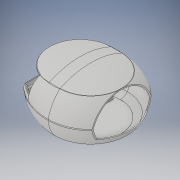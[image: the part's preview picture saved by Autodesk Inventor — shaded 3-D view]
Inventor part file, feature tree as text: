
AUTODESK INVENTOR PART (.ipt)
format: ipt  version: 2019 (Build 230136000, 136)  size: 2,652,672 bytes
history: native  units: mm
features: sketch x34, other x31, extrude x17, loft x12, pattern_linear x12, projected_geometry x12, fillet x10, mirror x5, revolve x3
ambient origin geometry x8: Origin, YZ Plane, XZ Plane, XY Plane, X Axis, Y Axis, Z Axis, Center Point
bodies: Body1 (feature_tree), Body2 (feature_tree)
feature tree (136):
  other  "голова"
  other  "Твердое тело1"
  sketch  "Эскиз1"
  extrude  "Выдавливание1"  Depth=42.3mm
  extrude  "Выдавливание2"  Depth=20.3mm
  extrude  "Выдавливание3"  Depth=40.0mm
  other  "РабПлоскость1"
  sketch  "Эскиз3"
  other  "РабПлоскость2"
  loft  "Лофт1"
  other  "РабПлоскость3"
  sketch  "Эскиз5"
  loft  "Лофт3"
  other  "РабПлоскость4"
  sketch  "Эскиз8"
  other  "РабПлоскость6"
  sketch  "Эскиз9"
  loft  "Лофт4"
  extrude  "Выдавливание4"  Depth=100.0mm
  mirror  "Зеркальное отражение1"
  loft  "Лофт5"
  loft  "Лофт6"
  loft  "Лофт7"
  sketch  "Эскиз11"
  extrude  "Выдавливание5"  Depth=20.0mm
  mirror  "Зеркальное отражение2"
  sketch  "Эскиз13"
  other  "РабПлоскость7"
  sketch  "Эскиз14"
  other  "РабПлоскость9"
  sketch  "Эскиз16"
  other  "РабПлоскость10"
  sketch  "Эскиз17"
  other  "РабПлоскость8"
  extrude  "Выдавливание6"  Depth=2.0mm TaperAngle=0.0deg
  loft  "Лофт8"
  mirror  "Зеркальное отражение3"
  other  "РабПлоскость11"
  revolve  "Вращение1"
  extrude  "Выдавливание7"  Depth=2.0mm
  loft  "Лофт9"
  loft  "Лофт10"
  other  "РабПлоскость12"
  sketch  "Эскиз20"
  sketch  "Эскиз21"
  sketch  "Эскиз22"
  loft  "Лофт11"
  loft  "Лофт12"
  mirror  "Зеркальное отражение4"
  other  "РабПлоскость13"
  loft  "Лофт13"
  extrude  "Выдавливание9"  Depth=50.0mm
  fillet  "Сопряжение1"  Radius=52.0mm
  fillet  "Сопряжение2"  Radius=2.0mm
  fillet  "Сопряжение3"  Radius=2.0mm
  fillet  "Сопряжение4"  Radius=46.0mm
  fillet  "Сопряжение5"  Radius=31.0mm
  fillet  "Сопряжение6"  Radius=30.0mm
  fillet  "Сопряжение7"  Radius=2.0mm
  extrude  "Выдавливание10"  Depth=2.0mm
  pattern_linear  "Прямоуг.массив1"  Spacing1=2.0mm  [1 undecoded]
  pattern_linear  "Прямоуг.массив2"  Spacing1=98.851581mm  [1 undecoded]
  pattern_linear  "Прямоуг.массив3"  Spacing1=40.790396mm  [1 undecoded]
  pattern_linear  "Прямоуг.массив4"  Spacing1=0.0mm  [1 undecoded]
  pattern_linear  "Прямоуг.массив5"  Spacing1=0.0mm  [1 undecoded]
  pattern_linear  "Прямоуг.массив6"  Spacing1=2.0mm  [1 undecoded]
  pattern_linear  "Прямоуг.массив7"  Spacing1=2.0mm  [1 undecoded]
  pattern_linear  "Прямоуг.массив8"  Spacing1=2.0mm  [1 undecoded]
  pattern_linear  "Прямоуг.массив9"  Spacing1=83.118457mm  [1 undecoded]
  pattern_linear  "Прямоуг.массив10"  Spacing1=1.99778mm  [1 undecoded]
  pattern_linear  "Прямоуг.массив11"  Spacing1=0.0mm  [1 undecoded]
  pattern_linear  "Прямоуг.массив12"  Spacing1=0.0mm  [1 undecoded]
  mirror  "Зеркальное отражение5"
  fillet  "Сопряжение8"  Radius=2.0mm
  fillet  "Сопряжение9"  Radius=2.0mm
  fillet  "Сопряжение10"  Radius=2.0mm
  extrude  "Выдавливание12"  Depth=53.0mm
  revolve  "Вращение2"
  extrude  "Выдавливание13"  Depth=2.0mm
  revolve  "Вращение3"
  other  "РабПлоскость14"
  sketch  "Эскиз35"
  extrude  "Выдавливание14"  TaperAngle=0.0deg  [1 undecoded]
  extrude  "Выдавливание15"  TaperAngle=0.0deg  [1 undecoded]
  other  "РабПлоскость15"
  extrude  "Выдавливание17"  TaperAngle=0.0deg  [1 undecoded]
  extrude  "Выдавливание20"  Depth=60.0mm TaperAngle=0.0deg
  sketch  "Эскиз47"
  extrude  "Выдавливание21"  TaperAngle=0.0deg  [1 undecoded]
  extrude  "Выдавливание22"  TaperAngle=0.0deg  [1 undecoded]
  sketch  "Эскиз2"
  sketch  "Эскиз4"
  projected_geometry  "Спроецированная петля1"
  other  "Ребра2"
  projected_geometry  "Спроецированная петля2"
  other  "Ребра3"
  other  "Ребра1"
  sketch  "Эскиз10"
  projected_geometry  "Спроецированная петля3"
  other  "Ребра4"
  other  "Ребра5"
  other  "Ребра6"
  other  "Ребра7"
  other  "Ребра8"
  other  "Ребра9"
  sketch  "Эскиз12"
  projected_geometry  "Спроецированная петля4"
  sketch  "Эскиз15"
  projected_geometry  "Спроецированная петля5"
  other  "Ребра10"
  sketch  "Эскиз18"
  sketch  "Эскиз19"
  projected_geometry  "Спроецированная петля6"
  other  "Ребра11"
  other  "Ребра12"
  other  "Ребра13"
  other  "Ребра14"
  projected_geometry  "Спроецированная петля7"
  projected_geometry  "Спроецированная петля8"
  other  "Ребра15"
  sketch  "Эскиз24"
  sketch  "Эскиз25"
  projected_geometry  "Спроецированная петля10"
  sketch  "Эскиз26"
  sketch  "Эскиз27"
  sketch  "Эскиз29"
  sketch  "Эскиз32"
  projected_geometry  "Спроецированная петля11"
  sketch  "Эскиз33"
  sketch  "Эскиз34"
  sketch  "Эскиз37"
  sketch  "Эскиз38"
  sketch  "Эскиз40"
  sketch  "Эскиз46"
  projected_geometry  "Спроецированная петля16"
  projected_geometry  "Спроецированная петля17"
note: 17 required parameter values undecoded (feature->parameter linkage not recoverable at this tier; creation-order binding heuristic only, values carry confidence <= 0.55)
